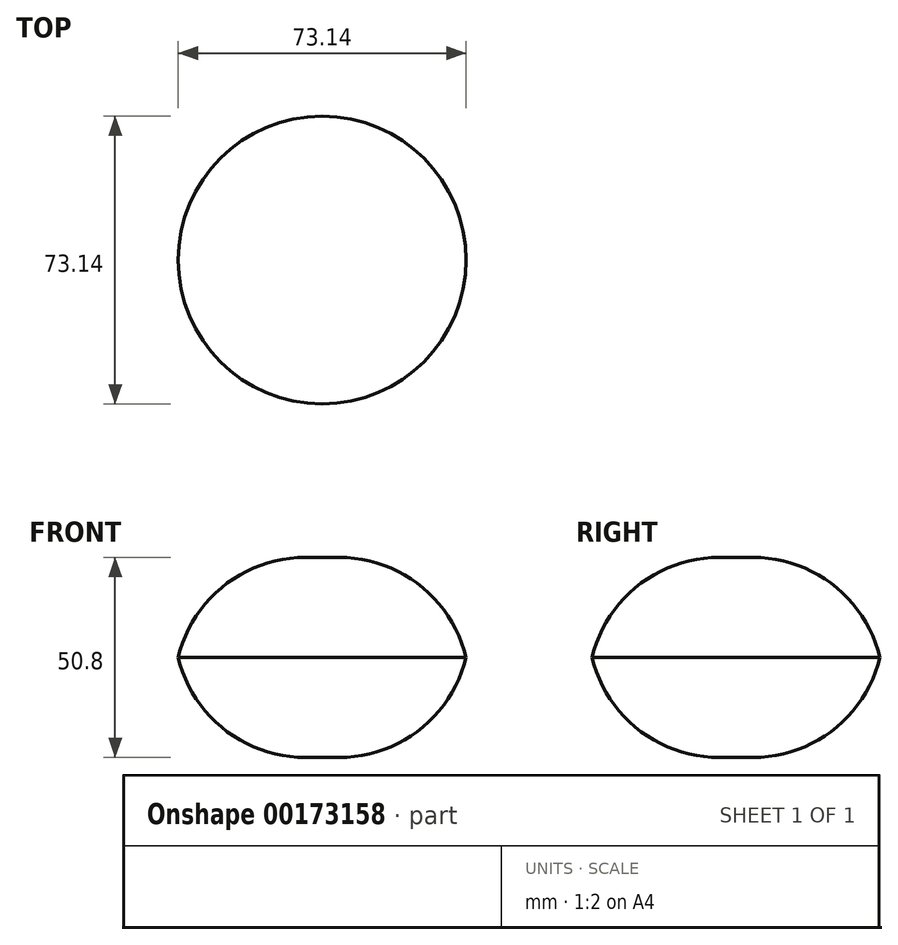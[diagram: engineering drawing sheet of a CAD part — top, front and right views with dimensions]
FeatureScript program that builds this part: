
annotation { "Feature Type Name" : "Feature", "Feature Type Description" : "" }
export const myFeature = defineFeature(function(context is Context, id is Id, definition is map)
    precondition{}
    {
        {
            var Q0;
            Q0=qCreatedBy(makeId("Top.planeOp"),FACE);
            var sketch = newSketch(context, id + "F0", { "sketchPlane" : qUnion([Q0])});
            skCircle(sketch, "E0", {"center": v(0, 0) * mm, "radius": 36.57 * mm});
            skSolve(sketch);
        }
        {
            var Q0;
            Q0=makeQuery(id+"F0.imprint","IMPRINT",FACE,{"disambiguationData":[TD([[makeQuery(id+"F0.imprint","IMPRINT",EDGE,{"derivedFrom":sQuery(id+"F0.wireOp",EDGE,"E0")}),1.0]])]});
            extrude(context, id + "F1", {"entities" : qUnion([Q0]), "depth" : 25.4 * mm});
        }
        {
            var Q0;
            Q0=makeQuery(id+"F1.opExtrude","CAP_EDGE",EDGE,{"disambiguationData":[OSD([sQuery(id+"F0.wireOp",EDGE,"E0")])],"isStart":false});
            fillet(context, id + "F2", {"entities" : qUnion([Q0]), "radius" : 33.1 * mm, "tangentPropagation" : true, "allowEdgeOverflow" : false});
        }
        {
            var Q0;
            Q0=makeQuery(id+"F1.opExtrude","SWEPT_BODY",BODY,{"disambiguationData":[OSD([sQuery(id+"F0.wireOp",EDGE,"E0")])]});
            var Q1;
            Q1=qCreatedBy(makeId("Top.planeOp"),FACE);
            mirror(context, id + "F3", {"operationType" : NewBodyOperationType.ADD, "entities" : qUnion([Q0]), "mirrorPlane" : qUnion([Q1])});
        }
    });
